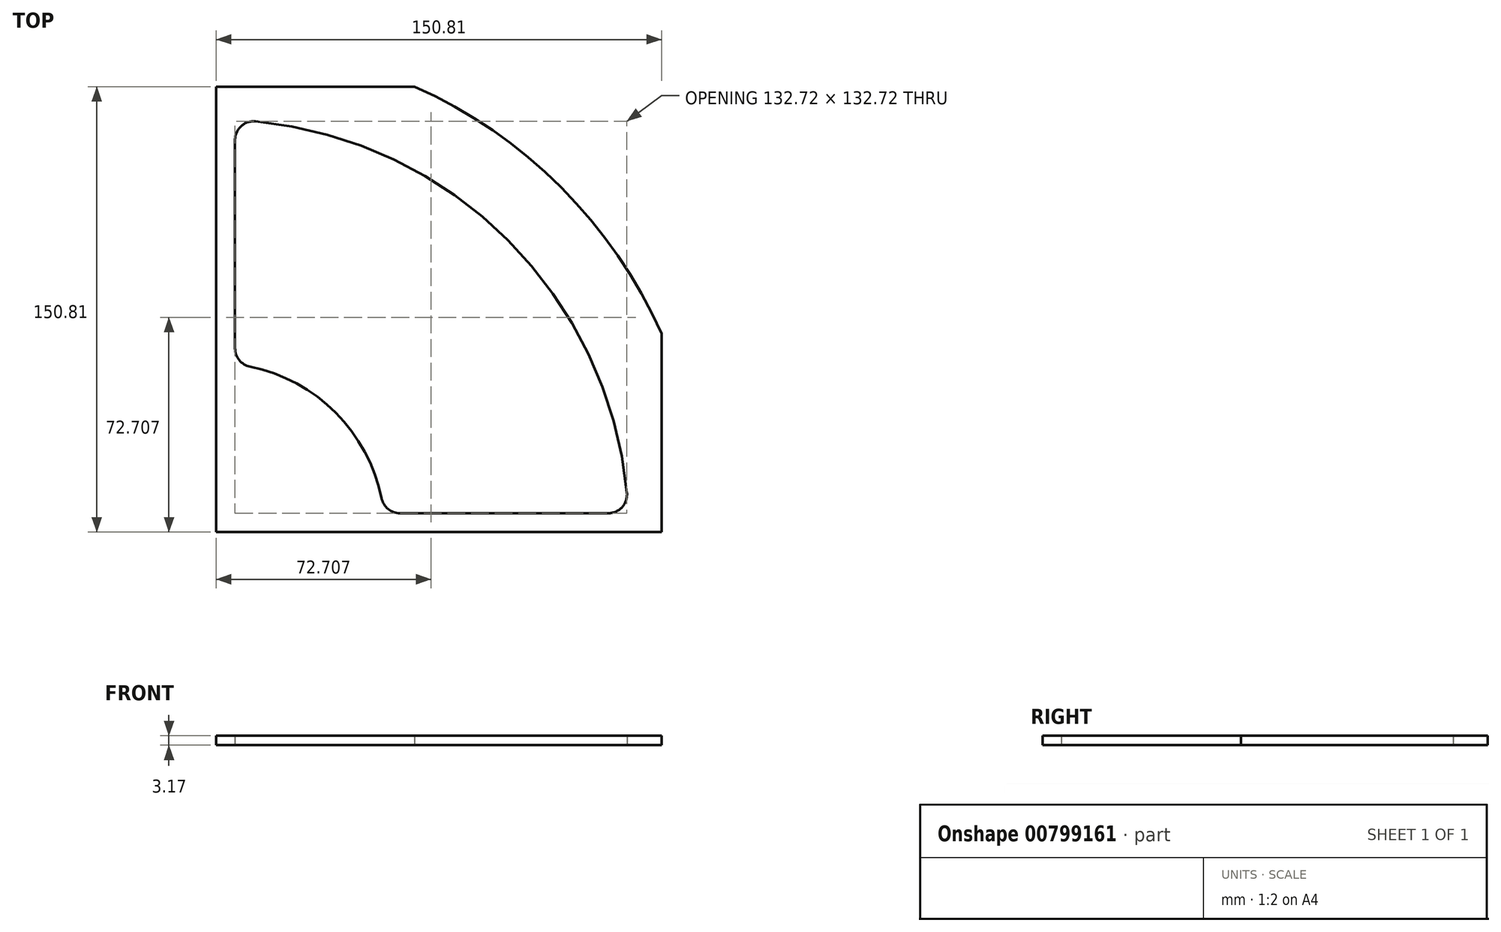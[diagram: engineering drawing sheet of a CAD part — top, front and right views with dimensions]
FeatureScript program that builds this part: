
annotation { "Feature Type Name" : "Feature", "Feature Type Description" : "" }
export const myFeature = defineFeature(function(context is Context, id is Id, definition is map)
    precondition{}
    {
        {
            var Q0;
            Q0=qCreatedBy(makeId("Top.planeOp"),FACE);
            var sketch = newSketch(context, id + "F0", { "sketchPlane" : qUnion([Q0])});
            skLineSegment(sketch, "E0", {"start": v(6.35, 62.22) * mm, "end": v(6.35, 132.74) * mm});
            skLineSegment(sketch, "E1", {"start": v(62.22, 6.35) * mm, "end": v(132.74, 6.35) * mm});
            skArc(sketch, "E2", {"start": v(56, 11.43) * mm, "mid": v(40.41, 40.41) * mm, "end": v(11.43, 56) * mm});
            skArc(sketch, "E3", {"start": v(139.06, 13.3) * mm, "mid": v(98.78, 98.78) * mm, "end": v(13.3, 139.06) * mm});
            skPoint(sketch, "E4.visualSharp", {"position": v(6.35, 139.56) * mm});
            skArc(sketch, "E4.filletArc", {"start": v(13.3, 139.06) * mm, "mid": v(8.43, 137.44) * mm, "end": v(6.35, 132.74) * mm});
            skPoint(sketch, "E5.visualSharp", {"position": v(139.56, 6.35) * mm});
            skArc(sketch, "E5.filletArc", {"start": v(132.74, 6.35) * mm, "mid": v(137.44, 8.43) * mm, "end": v(139.06, 13.3) * mm});
            skPoint(sketch, "E6.visualSharp", {"position": v(56.8, 6.35) * mm});
            skArc(sketch, "E6.filletArc", {"start": v(56, 11.43) * mm, "mid": v(58.2, 7.78) * mm, "end": v(62.22, 6.35) * mm});
            skPoint(sketch, "E7.visualSharp", {"position": v(6.35, 56.8) * mm});
            skArc(sketch, "E7.filletArc", {"start": v(6.35, 62.22) * mm, "mid": v(7.78, 58.2) * mm, "end": v(11.43, 56) * mm});
            skPoint(sketch, "E8", {"position": v(6.35, 62.22) * mm});
            skLineSegment(sketch, "E9", {"start": v(0, 0) * mm, "end": v(150.81, 0) * mm});
            skLineSegment(sketch, "E10", {"start": v(0, 0) * mm, "end": v(0, 150.81) * mm});
            skArc(sketch, "E11", {"start": v(150.81, 67.18) * mm, "mid": v(116.74, 116.74) * mm, "end": v(67.18, 150.81) * mm});
            skLineSegment(sketch, "E12", {"start": v(0, 150.81) * mm, "end": v(67.18, 150.81) * mm});
            skLineSegment(sketch, "E13", {"start": v(150.81, 0) * mm, "end": v(150.81, 67.18) * mm});
            skSolve(sketch);
        }
        {
            var Q0;
            Q0 = qSketchRegion(id + "F0", true);
            extrude(context, id + "F1", {"entities" : qUnion([Q0]), "depth" : 3.17 * mm, "offsetDistance" : 25.4 * mm});
        }
    });
